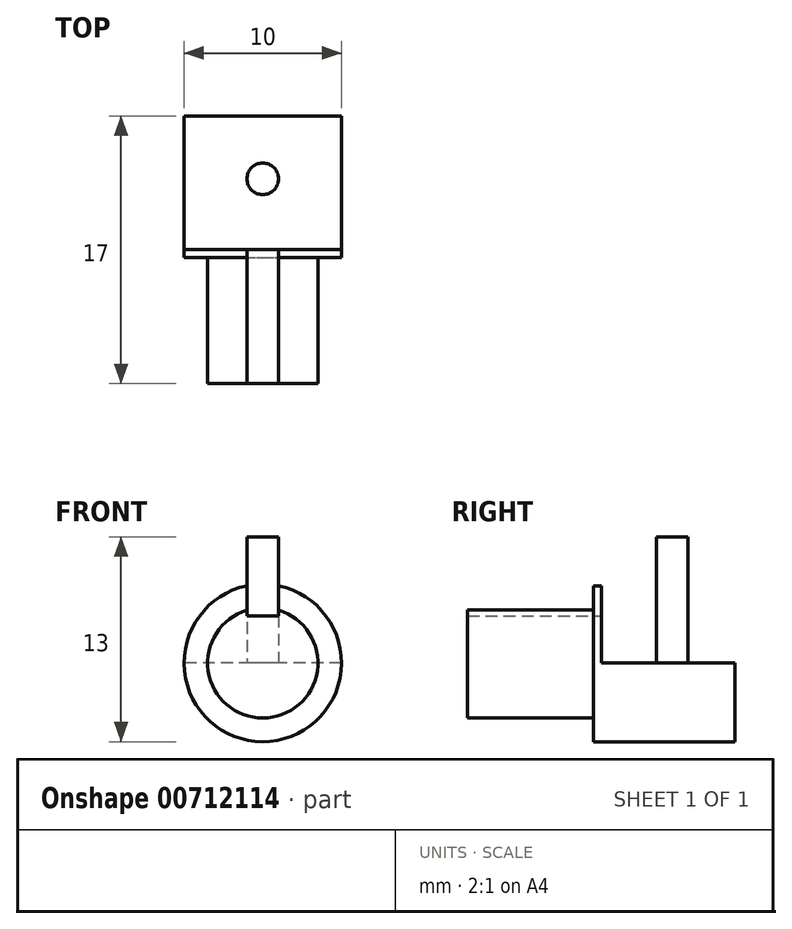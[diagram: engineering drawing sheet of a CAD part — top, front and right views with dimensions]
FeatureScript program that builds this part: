
annotation { "Feature Type Name" : "Feature", "Feature Type Description" : "" }
export const myFeature = defineFeature(function(context is Context, id is Id, definition is map)
    precondition{}
    {
        {
            var Q0;
            Q0=qCreatedBy(makeId("Front.planeOp"),FACE);
            var sketch = newSketch(context, id + "F0", { "sketchPlane" : qUnion([Q0])});
            skCircle(sketch, "E0", {"center": v(0, 0) * mm, "radius": 5 * mm});
            skSolve(sketch);
        }
        {
            var Q0;
            Q0 = qSketchRegion(id + "F0", true);
            extrude(context, id + "F1", {"entities" : qUnion([Q0]), "depth" : 9 * mm, "offsetDistance" : 25 * mm});
        }
        {
            var Q0;
            Q0=makeQuery(id+"F1.opExtrude","CAP_FACE",FACE,{"disambiguationData":[OSD([sQuery(id+"F0.wireOp",EDGE,"E0")])],"isStart":false});
            var sketch = newSketch(context, id + "F2", { "sketchPlane" : qUnion([Q0])});
            skCircle(sketch, "E1", {"center": v(0, 0) * mm, "radius": 3.5 * mm});
            skSolve(sketch);
        }
        {
            var Q0;
            Q0=makeQuery(id+"F2.imprint","IMPRINT",FACE,{"disambiguationData":[TD([[makeQuery(id+"F2.imprint","IMPRINT",EDGE,{"derivedFrom":sQuery(id+"F2.wireOp",EDGE,"E1")}),1.0]])]});
            extrude(context, id + "F3", {"entities" : qUnion([Q0]), "operationType" : NewBodyOperationType.ADD, "depth" : 8 * mm, "offsetDistance" : 25 * mm});
        }
        {
            var Q0;
            Q0=qCreatedBy(makeId("Right.planeOp"),FACE);
            var sketch = newSketch(context, id + "F4", { "sketchPlane" : qUnion([Q0])});
            skLineSegment(sketch, "E2.bottom", {"start": v(0.9, 0) * mm, "end": v(-8.5, 0) * mm});
            skLineSegment(sketch, "E2.top", {"start": v(0.9, 6) * mm, "end": v(-8.5, 6) * mm});
            skLineSegment(sketch, "E2.left", {"start": v(0.9, 0) * mm, "end": v(0.9, 6) * mm});
            skLineSegment(sketch, "E2.right", {"start": v(-8.5, 0) * mm, "end": v(-8.5, 6) * mm});
            skSolve(sketch);
        }
        {
            var Q0;
            Q0=makeQuery(id+"F4.imprint","IMPRINT",FACE,{"disambiguationData":[TD([[makeQuery(id+"F4.imprint","IMPRINT",EDGE,{"derivedFrom":sQuery(id+"F4.wireOp",EDGE,"E2.bottom")}),-1.0]])]});
            extrude(context, id + "F5", {"entities" : qUnion([Q0]), "operationType" : NewBodyOperationType.REMOVE, "oppositeDirection" : true, "depth" : 25 * mm, "offsetDistance" : 25 * mm, "symmetric" : true});
        }
        {
            var Q0;
            Q0=makeQuery(id+"F5.boolean.opBoolean","COPY",FACE,{"derivedFrom":makeQuery(id+"F5.opExtrude","SWEPT_FACE",FACE,{"disambiguationData":[OSD([sQuery(id+"F4.wireOp",EDGE,"E2.right")])]})});
            var sketch = newSketch(context, id + "F6", { "sketchPlane" : qUnion([Q0])});
            skLineSegment(sketch, "E3.bottom", {"start": v(1, 3) * mm, "end": v(-1, 3) * mm});
            skLineSegment(sketch, "E3.top", {"start": v(1, 9.62) * mm, "end": v(-1, 9.62) * mm});
            skLineSegment(sketch, "E3.left", {"start": v(1, 3) * mm, "end": v(1, 9.62) * mm});
            skLineSegment(sketch, "E3.right", {"start": v(-1, 3) * mm, "end": v(-1, 9.62) * mm});
            skPoint(sketch, "E3.middle", {"position": v(0, 6.3) * mm});
            skSolve(sketch);
        }
        {
            var Q0;
            {var subQ0=sQuery(id+"F6.wireOp",EDGE,"E3.bottom");Q0=makeQuery(id+"F6.imprint","IMPRINT",FACE,{"disambiguationData":[TD([[makeQuery(id+"F6.imprint","IMPRINT",EDGE,{"derivedFrom":subQ0}),-1.0]])]});}
            extrude(context, id + "F7", {"entities" : qUnion([Q0]), "operationType" : NewBodyOperationType.REMOVE, "oppositeDirection" : true, "depth" : 25 * mm, "offsetDistance" : 25 * mm});
        }
        {
            var Q0;
            Q0=makeQuery(id+"F5.boolean.opBoolean","COPY",FACE,{"derivedFrom":makeQuery(id+"F5.opExtrude","SWEPT_FACE",FACE,{"disambiguationData":[OSD([sQuery(id+"F4.wireOp",EDGE,"E2.bottom")])]})});
            var sketch = newSketch(context, id + "F8", { "sketchPlane" : qUnion([Q0])});
            skLineSegment(sketch, "E4", {"start": v(-10, -4) * mm, "end": v(11.38, -4) * mm, "construction": true});
            skPoint(sketch, "E5", {"position": v(0, -4) * mm});
            skCircle(sketch, "E6", {"center": v(0, -4) * mm, "radius": 1 * mm});
            skSolve(sketch);
        }
        {
            var Q0;
            Q0 = qSketchRegion(id + "F8", true);
            extrude(context, id + "F9", {"entities" : qUnion([Q0]), "operationType" : NewBodyOperationType.ADD, "depth" : 8 * mm, "offsetDistance" : 25 * mm});
        }
    });
